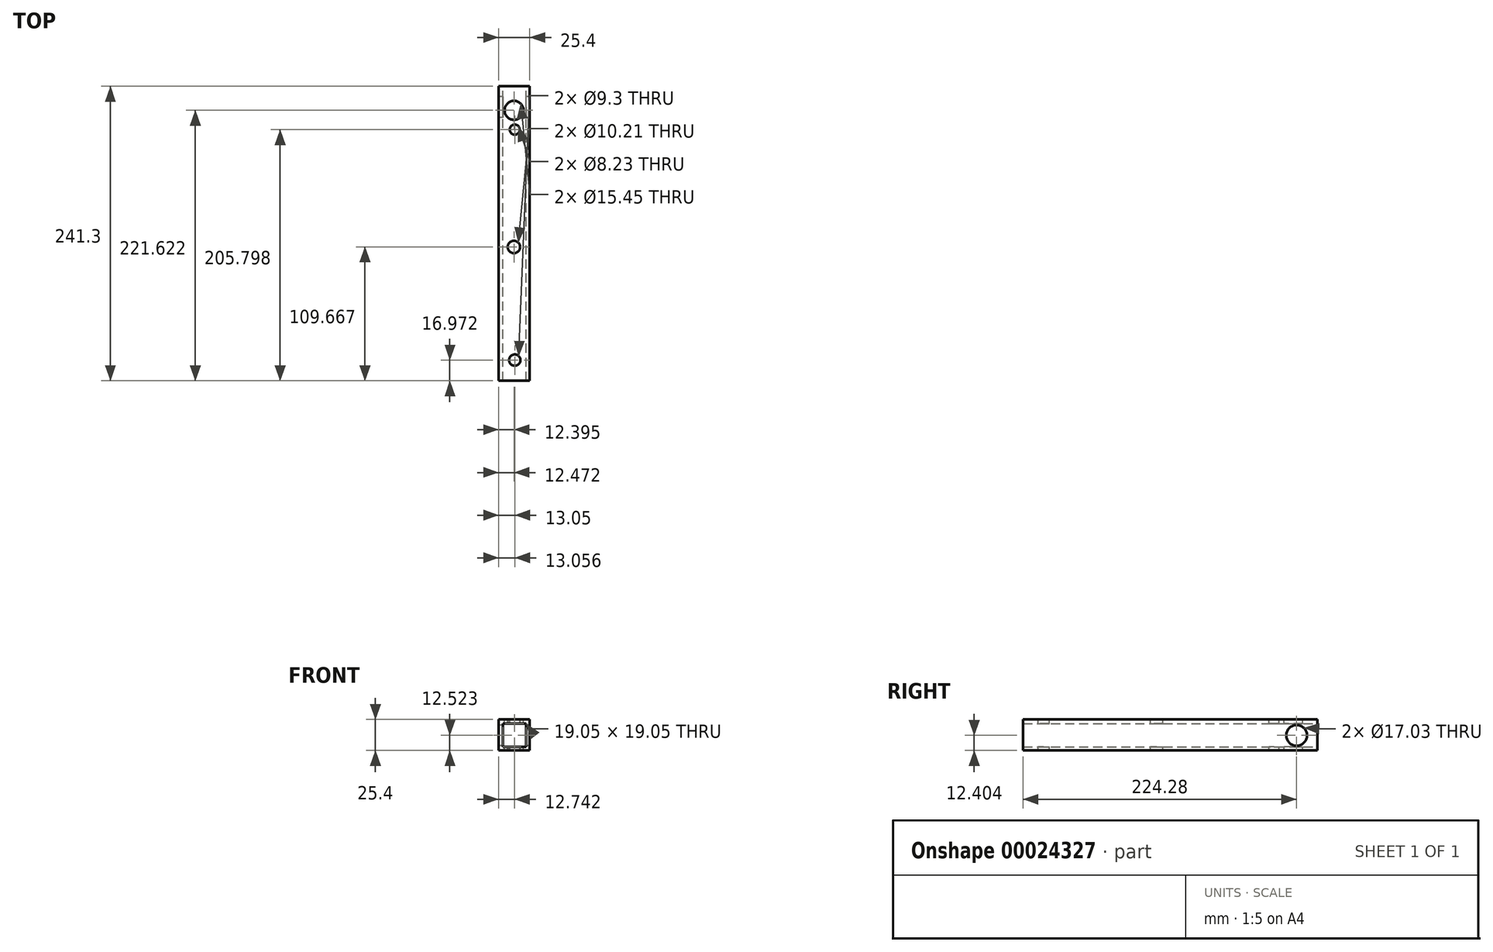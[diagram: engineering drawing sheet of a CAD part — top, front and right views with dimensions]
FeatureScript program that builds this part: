
annotation { "Feature Type Name" : "Feature", "Feature Type Description" : "" }
export const myFeature = defineFeature(function(context is Context, id is Id, definition is map)
    precondition{}
    {
        {
            var Q0;
            Q0=qCreatedBy(makeId("Top.planeOp"),FACE);
            var sketch = newSketch(context, id + "F0", { "sketchPlane" : qUnion([Q0])});
            skLineSegment(sketch, "E0", {"start": v(-46.95, 204.33) * mm, "end": v(-46.95, -36.97) * mm});
            skLineSegment(sketch, "E1", {"start": v(-46.95, -36.97) * mm, "end": v(-21.55, -36.97) * mm});
            skLineSegment(sketch, "E2", {"start": v(-21.55, -36.97) * mm, "end": v(-21.55, 204.33) * mm});
            skLineSegment(sketch, "E3", {"start": v(-21.55, 204.33) * mm, "end": v(-46.95, 204.33) * mm});
            skSolve(sketch);
        }
        {
            var Q0;
            Q0=makeQuery(id+"F0.imprint","IMPRINT",FACE,{"disambiguationData":[TD([[makeQuery(id+"F0.imprint","IMPRINT",EDGE,{"derivedFrom":sQuery(id+"F0.wireOp",EDGE,"E0")}),1.0]])]});
            extrude(context, id + "F1", {"entities" : qUnion([Q0]), "depth" : 25.4 * mm});
        }
        {
            var Q0;
            Q0=makeQuery(id+"F1.opExtrude","SWEPT_FACE",FACE,{"disambiguationData":[OSD([sQuery(id+"F0.wireOp",EDGE,"E3")])]});
            var sketch = newSketch(context, id + "F2", { "sketchPlane" : qUnion([Q0])});
            skLineSegment(sketch, "E4", {"start": v(24.68, 22.05) * mm, "end": v(24.68, 3) * mm});
            skLineSegment(sketch, "E5", {"start": v(24.68, 3) * mm, "end": v(43.73, 3) * mm});
            skLineSegment(sketch, "E6", {"start": v(43.73, 3) * mm, "end": v(43.73, 22.05) * mm});
            skLineSegment(sketch, "E7", {"start": v(43.73, 22.05) * mm, "end": v(24.68, 22.05) * mm});
            skSolve(sketch);
        }
        {
            var Q0;
            Q0=makeQuery(id+"F2.imprint","IMPRINT",FACE,{"disambiguationData":[TD([[makeQuery(id+"F2.imprint","IMPRINT",EDGE,{"derivedFrom":sQuery(id+"F2.wireOp",EDGE,"E4")}),1.0]])]});
            extrude(context, id + "F3", {"entities" : qUnion([Q0]), "operationType" : NewBodyOperationType.REMOVE, "oppositeDirection" : true, "depth" : 255.84 * mm});
        }
        {
            var Q0;
            Q0=makeQuery(id+"F1.opExtrude","CAP_FACE",FACE,{"disambiguationData":[OSD([sQuery(id+"F0.wireOp",EDGE,"E0"),sQuery(id+"F0.wireOp",EDGE,"E1"),sQuery(id+"F0.wireOp",EDGE,"E2"),sQuery(id+"F0.wireOp",EDGE,"E3")])],"isStart":false});
            var sketch = newSketch(context, id + "F4", { "sketchPlane" : qUnion([Q0])});
            skCircle(sketch, "E8", {"center": v(-34.48, 184.65) * mm, "radius": 7.73 * mm});
            skCircle(sketch, "E9", {"center": v(-33.9, 168.83) * mm, "radius": 4.12 * mm});
            skCircle(sketch, "E10", {"center": v(-34.55, 72.7) * mm, "radius": 5.1 * mm});
            skSolve(sketch);
        }
        {
            var Q0;
            Q0=makeQuery(id+"F4.imprint","IMPRINT",FACE,{"disambiguationData":[TD([[makeQuery(id+"F4.imprint","IMPRINT",EDGE,{"derivedFrom":sQuery(id+"F4.wireOp",EDGE,"E8")}),-1.0]])]});
            var sketch = newSketch(context, id + "F5", { "sketchPlane" : qUnion([Q0])});
            skCircle(sketch, "E11", {"center": v(-33.9, -20) * mm, "radius": 4.65 * mm});
            skSolve(sketch);
        }
        {
            var Q0;
            Q0=makeQuery(id+"F4.imprint","IMPRINT",FACE,{"disambiguationData":[TD([[makeQuery(id+"F4.imprint","IMPRINT",EDGE,{"derivedFrom":sQuery(id+"F4.wireOp",EDGE,"E8")}),1.0]])]});
            var Q1;
            Q1=makeQuery(id+"F4.imprint","IMPRINT",FACE,{"disambiguationData":[TD([[makeQuery(id+"F4.imprint","IMPRINT",EDGE,{"derivedFrom":sQuery(id+"F4.wireOp",EDGE,"E9")}),1.0]])]});
            var Q2;
            Q2=makeQuery(id+"F4.imprint","IMPRINT",FACE,{"disambiguationData":[TD([[makeQuery(id+"F4.imprint","IMPRINT",EDGE,{"derivedFrom":sQuery(id+"F4.wireOp",EDGE,"E10")}),1.0]])]});
            var Q3;
            Q3=makeQuery(id+"F5.imprint","IMPRINT",FACE,{"disambiguationData":[TD([[makeQuery(id+"F5.imprint","IMPRINT",EDGE,{"derivedFrom":sQuery(id+"F5.wireOp",EDGE,"E11")}),1.0]])]});
            extrude(context, id + "F6", {"entities" : qUnion([Q0, Q1, Q2, Q3]), "operationType" : NewBodyOperationType.REMOVE, "oppositeDirection" : true, "depth" : 73.48 * mm});
        }
        {
            var Q0;
            Q0=makeQuery(id+"F1.opExtrude","SWEPT_FACE",FACE,{"disambiguationData":[OSD([sQuery(id+"F0.wireOp",EDGE,"E0")])]});
            var sketch = newSketch(context, id + "F7", { "sketchPlane" : qUnion([Q0])});
            skCircle(sketch, "E12", {"center": v(-187.31, 12.4) * mm, "radius": 8.51 * mm});
            skSolve(sketch);
        }
        {
            var Q0;
            Q0 = qSketchRegion(id + "F7", true);
            extrude(context, id + "F8", {"entities" : qUnion([Q0]), "operationType" : NewBodyOperationType.REMOVE, "oppositeDirection" : true, "depth" : 25.4 * mm});
        }
    });
